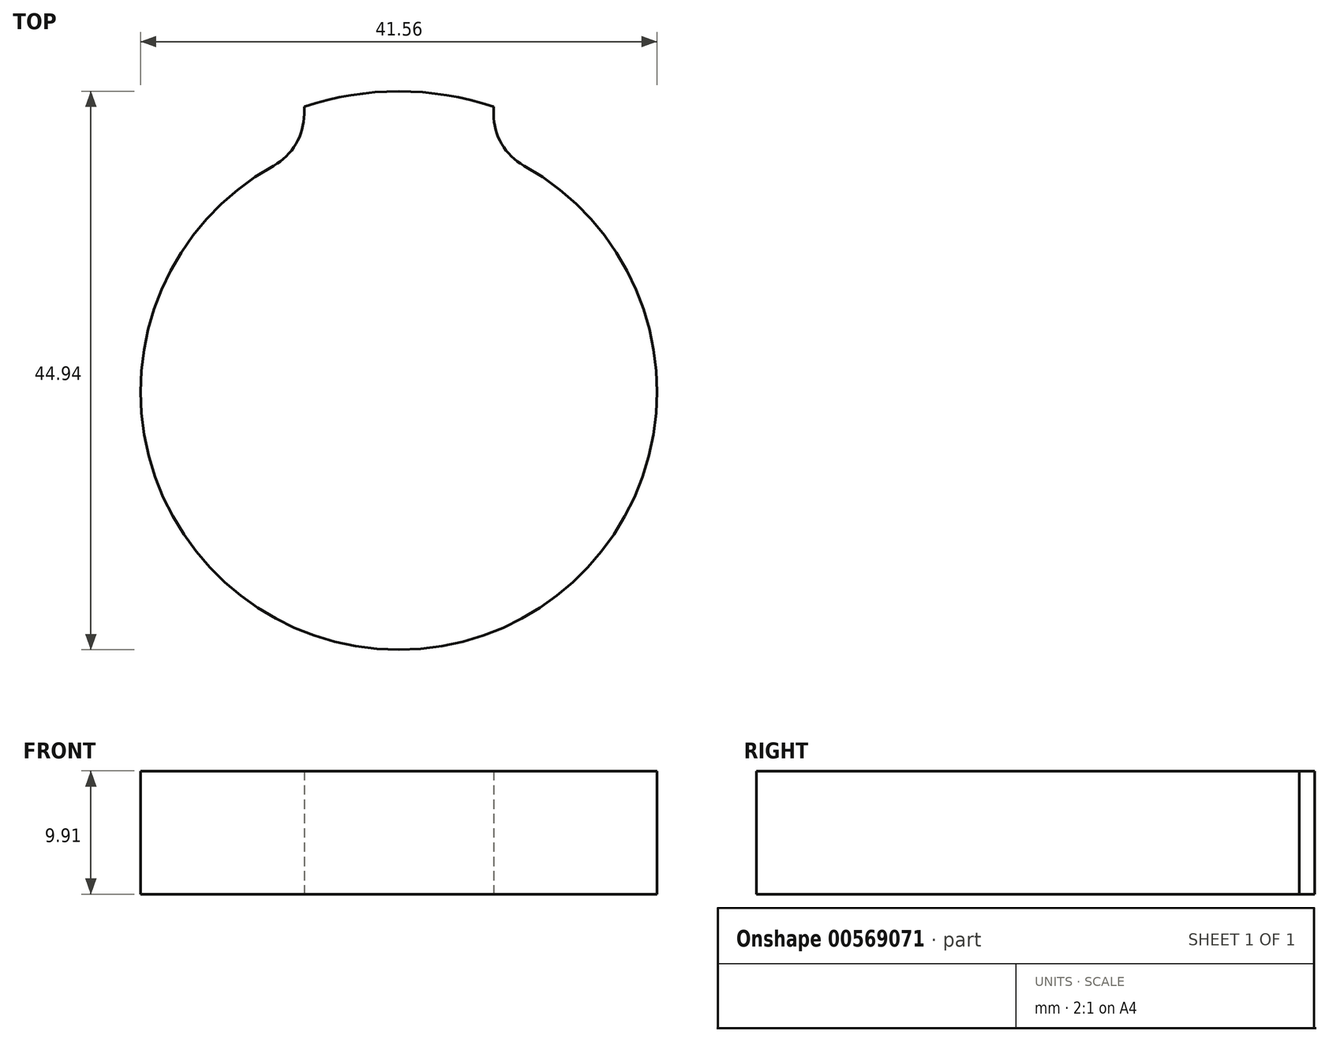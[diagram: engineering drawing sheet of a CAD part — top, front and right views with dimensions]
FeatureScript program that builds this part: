
annotation { "Feature Type Name" : "Feature", "Feature Type Description" : "" }
export const myFeature = defineFeature(function(context is Context, id is Id, definition is map)
    precondition{}
    {
        {
            var Q0;
            Q0=qCreatedBy(makeId("Top.planeOp"),FACE);
            var sketch = newSketch(context, id + "F0", { "sketchPlane" : qUnion([Q0])});
            skCircle(sketch, "E0", {"center": v(0, 0) * mm, "radius": 20.78 * mm});
            skArc(sketch, "E1", {"start": v(0, 24.16) * mm, "mid": v(-3.86, 23.85) * mm, "end": v(-7.62, 22.92) * mm});
            skLineSegment(sketch, "E2", {"start": v(-7.62, 22.92) * mm, "end": v(-7.62, 19.33) * mm});
            skArc(sketch, "E3.MirrorCS", {"start": v(0, 24.16) * mm, "mid": v(3.86, 23.85) * mm, "end": v(7.62, 22.92) * mm});
            skLineSegment(sketch, "E4.MirrorCS", {"start": v(7.62, 22.92) * mm, "end": v(7.62, 19.33) * mm});
            skSolve(sketch);
        }
        {
            var Q0;
            {var subQ0=sQuery(id+"F0.wireOp",EDGE,"E0");var subQ1=makeQuery(id+"F0.imprint","INTERSECT",VERTEX,{"derivedFrom":[subQ0,sQuery(id+"F0.wireOp",EDGE,"E2")]});Q0=makeQuery(id+"F0.imprint","IMPRINT",FACE,{"disambiguationData":[TD([[makeQuery(id+"F0.imprint","IMPRINT",EDGE,{"disambiguationData":[TD([[subQ1,1.0]])],"derivedFrom":subQ0}),1.0]])]});}
            var Q1;
            Q1=makeQuery(id+"F0.imprint","IMPRINT",FACE,{"disambiguationData":[TD([[makeQuery(id+"F0.imprint","IMPRINT",EDGE,{"derivedFrom":sQuery(id+"F0.wireOp",EDGE,"E1")}),1.0]])]});
            extrude(context, id + "F1", {"entities" : qUnion([Q0, Q1]), "depth" : 9.9 * mm, "offsetDistance" : 25.4 * mm});
        }
        {
            var Q0;
            Q0=makeQuery(id+"F1.opExtrude","SWEPT_EDGE",EDGE,{"disambiguationData":[OSD([sQuery(id+"F0.wireOp",EDGE,"E0"),sQuery(id+"F0.wireOp",EDGE,"E4.MirrorCS")])]});
            var Q1;
            Q1=makeQuery(id+"F1.opExtrude","SWEPT_EDGE",EDGE,{"disambiguationData":[OSD([sQuery(id+"F0.wireOp",EDGE,"E0"),sQuery(id+"F0.wireOp",EDGE,"E2")])]});
            fillet(context, id + "F2", {"entities" : qUnion([Q0, Q1]), "radius" : 4.76 * mm, "tangentPropagation" : true, "allowEdgeOverflow" : false});
        }
    });
